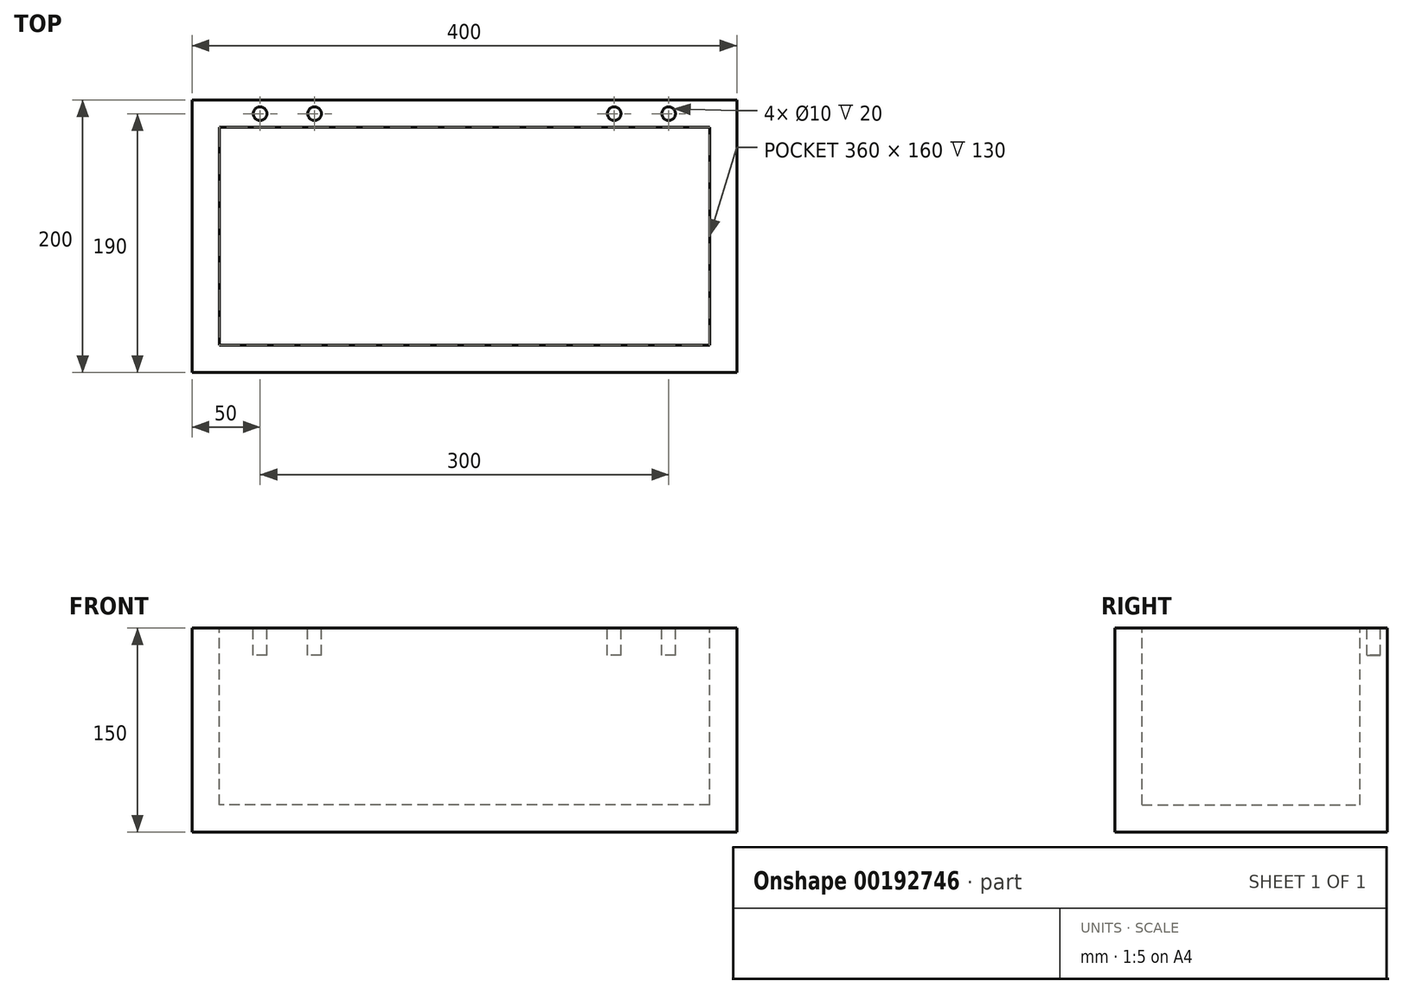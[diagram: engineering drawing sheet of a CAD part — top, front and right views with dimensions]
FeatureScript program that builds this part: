
annotation { "Feature Type Name" : "Feature", "Feature Type Description" : "" }
export const myFeature = defineFeature(function(context is Context, id is Id, definition is map)
    precondition{}
    {
        {
            var Q0;
            Q0=qCreatedBy(makeId("Top.planeOp"),FACE);
            var sketch = newSketch(context, id + "F0", { "sketchPlane" : qUnion([Q0])});
            skLineSegment(sketch, "E0.bottom", {"start": v(200, -100) * mm, "end": v(-200, -100) * mm});
            skLineSegment(sketch, "E0.top", {"start": v(200, 100) * mm, "end": v(-200, 100) * mm});
            skLineSegment(sketch, "E0.left", {"start": v(200, -100) * mm, "end": v(200, 100) * mm});
            skLineSegment(sketch, "E0.right", {"start": v(-200, -100) * mm, "end": v(-200, 100) * mm});
            skPoint(sketch, "E0.middle", {"position": v(0, 0) * mm});
            skSolve(sketch);
        }
        {
            var Q0;
            Q0 = qSketchRegion(id + "F0", true);
            extrude(context, id + "F1", {"entities" : qUnion([Q0]), "depth" : 150 * mm});
        }
        {
            var Q0;
            Q0=makeQuery(id+"F1.opExtrude","CAP_FACE",FACE,{"disambiguationData":[OSD([sQuery(id+"F0.wireOp",EDGE,"E0.bottom"),sQuery(id+"F0.wireOp",EDGE,"E0.top"),sQuery(id+"F0.wireOp",EDGE,"E0.left"),sQuery(id+"F0.wireOp",EDGE,"E0.right")])],"isStart":false});
            var sketch = newSketch(context, id + "F2", { "sketchPlane" : qUnion([Q0])});
            skLineSegment(sketch, "E1.bottom", {"start": v(180, -80) * mm, "end": v(-180, -80) * mm});
            skLineSegment(sketch, "E1.top", {"start": v(180, 80) * mm, "end": v(-180, 80) * mm});
            skLineSegment(sketch, "E1.left", {"start": v(180, -80) * mm, "end": v(180, 80) * mm});
            skLineSegment(sketch, "E1.right", {"start": v(-180, -80) * mm, "end": v(-180, 80) * mm});
            skPoint(sketch, "E1.middle", {"position": v(0, 0) * mm});
            skSolve(sketch);
        }
        {
            var Q0;
            Q0=makeQuery(id+"F2.imprint","IMPRINT",FACE,{"disambiguationData":[TD([[makeQuery(id+"F2.imprint","IMPRINT",EDGE,{"derivedFrom":sQuery(id+"F2.wireOp",EDGE,"E1.bottom")}),-1.0]])]});
            extrude(context, id + "F3", {"entities" : qUnion([Q0]), "operationType" : NewBodyOperationType.REMOVE, "oppositeDirection" : true, "depth" : 130 * mm});
        }
        {
            var Q0;
            Q0=makeQuery(id+"F1.opExtrude","CAP_FACE",FACE,{"disambiguationData":[OSD([sQuery(id+"F0.wireOp",EDGE,"E0.bottom"),sQuery(id+"F0.wireOp",EDGE,"E0.top"),sQuery(id+"F0.wireOp",EDGE,"E0.left"),sQuery(id+"F0.wireOp",EDGE,"E0.right")])],"isStart":false});
            var sketch = newSketch(context, id + "F4", { "sketchPlane" : qUnion([Q0])});
            skCircle(sketch, "E2", {"center": v(-150, 90) * mm, "radius": 5 * mm});
            skCircle(sketch, "E3", {"center": v(-110, 90) * mm, "radius": 5 * mm});
            skLineSegment(sketch, "E4", {"start": v(0, 80) * mm, "end": v(0, 100) * mm, "construction": true});
            skCircle(sketch, "E5.MirrorC", {"center": v(110, 90) * mm, "radius": 5 * mm});
            skCircle(sketch, "E6.MirrorC", {"center": v(150, 90) * mm, "radius": 5 * mm});
            skSolve(sketch);
        }
        {
            var Q0;
            Q0 = qSketchRegion(id + "F4", true);
            extrude(context, id + "F5", {"entities" : qUnion([Q0]), "operationType" : NewBodyOperationType.REMOVE, "oppositeDirection" : true, "depth" : 20 * mm});
        }
    });
